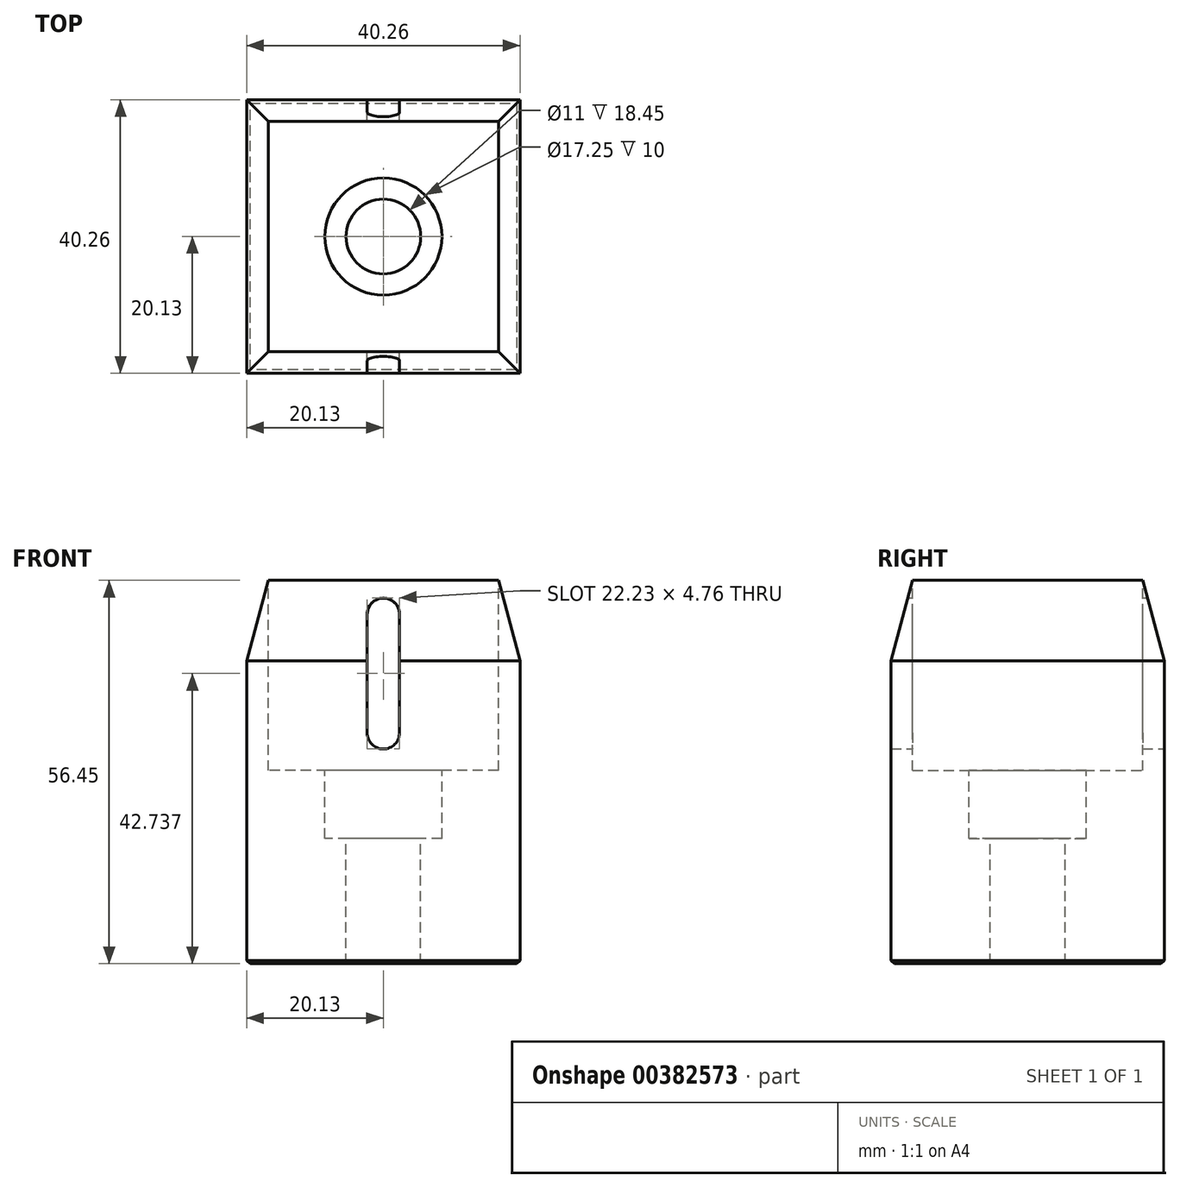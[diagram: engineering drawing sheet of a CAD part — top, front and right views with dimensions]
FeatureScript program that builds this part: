
annotation { "Feature Type Name" : "Feature", "Feature Type Description" : "" }
export const myFeature = defineFeature(function(context is Context, id is Id, definition is map)
    precondition{}
    {
        {
            var Q0;
            Q0=qCreatedBy(makeId("Top.planeOp"),FACE);
            var sketch = newSketch(context, id + "F0", { "sketchPlane" : qUnion([Q0])});
            skLineSegment(sketch, "E0.bottom", {"start": v(20.12, -20.12) * mm, "end": v(-20.13, -20.13) * mm});
            skLineSegment(sketch, "E0.top", {"start": v(20.12, 20.12) * mm, "end": v(-20.13, 20.12) * mm});
            skLineSegment(sketch, "E0.left", {"start": v(20.12, -20.12) * mm, "end": v(20.12, 20.13) * mm});
            skLineSegment(sketch, "E0.right", {"start": v(-20.13, -20.13) * mm, "end": v(-20.13, 20.12) * mm});
            skPoint(sketch, "E0.middle", {"position": v(0, 0) * mm});
            skSolve(sketch);
        }
        {
            var Q0;
            Q0=qSketchRegion(id+"F0",true);
            extrude(context, id + "F1", {"entities" : qUnion([Q0]), "depth" : 56.45 * mm});
        }
        {
            var Q0;
            Q0=makeQuery(id+"F1.opExtrude","CAP_FACE",FACE,{"disambiguationData":[OSD([sQuery(id+"F0.wireOp",EDGE,"E0.bottom"),sQuery(id+"F0.wireOp",EDGE,"E0.top"),sQuery(id+"F0.wireOp",EDGE,"E0.left"),sQuery(id+"F0.wireOp",EDGE,"E0.right")])],"isStart":false});
            var sketch = newSketch(context, id + "F2", { "sketchPlane" : qUnion([Q0])});
            skLineSegment(sketch, "E1.bottom", {"start": v(16.95, -16.95) * mm, "end": v(-16.95, -16.95) * mm});
            skLineSegment(sketch, "E1.top", {"start": v(16.95, 16.95) * mm, "end": v(-16.95, 16.95) * mm});
            skLineSegment(sketch, "E1.left", {"start": v(16.95, -16.95) * mm, "end": v(16.95, 16.95) * mm});
            skLineSegment(sketch, "E1.right", {"start": v(-16.95, -16.95) * mm, "end": v(-16.95, 16.95) * mm});
            skPoint(sketch, "E1.middle", {"position": v(0, 0) * mm});
            skSolve(sketch);
        }
        {
            var Q0;
            Q0=qSketchRegion(id+"F2",true);
            extrude(context, id + "F3", {"entities" : qUnion([Q0]), "operationType" : NewBodyOperationType.REMOVE, "oppositeDirection" : true, "depth" : 28 * mm});
        }
        {
            var Q0;
            Q0=makeQuery(id+"F3.boolean.opBoolean","COPY",FACE,{"derivedFrom":makeQuery(id+"F3.opExtrude","CAP_FACE",FACE,{"disambiguationData":[OSD([sQuery(id+"F2.wireOp",EDGE,"E1.bottom"),sQuery(id+"F2.wireOp",EDGE,"E1.top"),sQuery(id+"F2.wireOp",EDGE,"E1.left"),sQuery(id+"F2.wireOp",EDGE,"E1.right")])],"isStart":false})});
            var sketch = newSketch(context, id + "F4", { "sketchPlane" : qUnion([Q0])});
            skPoint(sketch, "E2", {"position": v(0, 0) * mm});
            skSolve(sketch);
        }
        {
            var Q0;
            Q0=sQuery(id+"F4.wireOp",VERTEX,"E2");
            var Q1;
            Q1=makeQuery(id+"F1.opExtrude","SWEPT_BODY",BODY,{"disambiguationData":[OSD([sQuery(id+"F0.wireOp",EDGE,"E0.bottom"),sQuery(id+"F0.wireOp",EDGE,"E0.top"),sQuery(id+"F0.wireOp",EDGE,"E0.left"),sQuery(id+"F0.wireOp",EDGE,"E0.right")])]});
            hole(context, id + "F5", {"style" : HoleStyle.C_BORE, "endStyle" : HoleEndStyle.THROUGH, "standardTappedOrClearance" : lookupTablePath({ "standard" : "ISO", "fit" : "Normal", "size" : "M10", "type" : "Clearance" }), "standardBlindInLast" : lookupTablePath({ "fit" : "Standard", "standard" : "ISO", "size" : "M10", "type" : "Clearance" }), "holeDiameter" : 11 * mm, "cBoreDiameter" : 17.25 * mm, "cBoreDepth" : 10 * mm, "isTappedThrough" : true, "tappedDepth" : 12.7 * mm, "tapClearance" : 3, "locations" : qUnion([Q0]), "scope" : qUnion([Q1])});
        }
        {
            var Q0;
            Q0=makeQuery(id+"F1.opExtrude","CAP_EDGE",EDGE,{"disambiguationData":[OSD([sQuery(id+"F0.wireOp",EDGE,"E0.top")])],"isStart":false});
            var Q1;
            Q1=makeQuery(id+"F1.opExtrude","CAP_EDGE",EDGE,{"disambiguationData":[OSD([sQuery(id+"F0.wireOp",EDGE,"E0.left")])],"isStart":false});
            var Q2;
            Q2=makeQuery(id+"F1.opExtrude","CAP_EDGE",EDGE,{"disambiguationData":[OSD([sQuery(id+"F0.wireOp",EDGE,"E0.bottom")])],"isStart":false});
            var Q3;
            Q3=makeQuery(id+"F1.opExtrude","CAP_EDGE",EDGE,{"disambiguationData":[OSD([sQuery(id+"F0.wireOp",EDGE,"E0.right")])],"isStart":false});
            chamfer(context, id + "F6", {"entities" : qUnion([Q0, Q1, Q2, Q3]), "chamferType" : ChamferType.OFFSET_ANGLE, "width" : 3.17 * mm, "oppositeDirection" : false, "angle" : 75 * degree, "tangentPropagation" : true});
        }
        {
            var Q0;
            Q0=makeQuery(id+"F1.opExtrude","SWEPT_FACE",FACE,{"disambiguationData":[OSD([sQuery(id+"F0.wireOp",EDGE,"E0.top")])]});
            cPlane(context, id + "F7", {"entities" : qUnion([Q0]), "cplaneType" : CPlaneType.OFFSET, "offset" : 0 * mm, "width" : 152.4 * mm, "height" : 152.4 * mm});
        }
        {
            var Q0;
            Q0=qCreatedBy(id+"F7.planeOp",FACE);
            var sketch = newSketch(context, id + "F8", { "sketchPlane" : qUnion([Q0])});
            skLineSegment(sketch, "E3", {"start": v(0, 71.95) * mm, "end": v(0, 0) * mm, "construction": true});
            skLineSegment(sketch, "E4.bottom", {"start": v(2.38, 34) * mm, "end": v(-2.38, 34) * mm});
            skLineSegment(sketch, "E4.top", {"start": v(2.38, 51.47) * mm, "end": v(-2.38, 51.47) * mm});
            skLineSegment(sketch, "E4.left", {"start": v(2.38, 34) * mm, "end": v(2.38, 51.47) * mm});
            skLineSegment(sketch, "E4.right", {"start": v(-2.38, 34) * mm, "end": v(-2.38, 51.47) * mm});
            skPoint(sketch, "E4.middle", {"position": v(0, 42.74) * mm});
            skArc(sketch, "E5", {"start": v(-2.38, 51.47) * mm, "mid": v(0, 53.85) * mm, "end": v(2.38, 51.47) * mm});
            skArc(sketch, "E6", {"start": v(-2.38, 34) * mm, "mid": v(0, 31.63) * mm, "end": v(2.38, 34) * mm});
            skSolve(sketch);
        }
        {
            var Q0;
            Q0=qSketchRegion(id+"F8",true);
            extrude(context, id + "F9", {"entities" : qUnion([Q0]), "operationType" : NewBodyOperationType.REMOVE, "endBound" : BoundingType.THROUGH_ALL, "oppositeDirection" : true, "depth" : 25.4 * mm});
        }
        {
            var Q0;
            Q0=makeQuery(id+"F1.opExtrude","CAP_EDGE",EDGE,{"disambiguationData":[OSD([sQuery(id+"F0.wireOp",EDGE,"E0.left")])],"isStart":true});
            var Q1;
            Q1=makeQuery(id+"F1.opExtrude","CAP_EDGE",EDGE,{"disambiguationData":[OSD([sQuery(id+"F0.wireOp",EDGE,"E0.bottom")])],"isStart":true});
            var Q2;
            Q2=makeQuery(id+"F1.opExtrude","CAP_EDGE",EDGE,{"disambiguationData":[OSD([sQuery(id+"F0.wireOp",EDGE,"E0.right")])],"isStart":true});
            var Q3;
            Q3=makeQuery(id+"F1.opExtrude","CAP_EDGE",EDGE,{"disambiguationData":[OSD([sQuery(id+"F0.wireOp",EDGE,"E0.top")])],"isStart":true});
            chamfer(context, id + "F10", {"entities" : qUnion([Q0, Q1, Q2, Q3]), "width" : .5 * mm, "tangentPropagation" : true});
        }
    });
